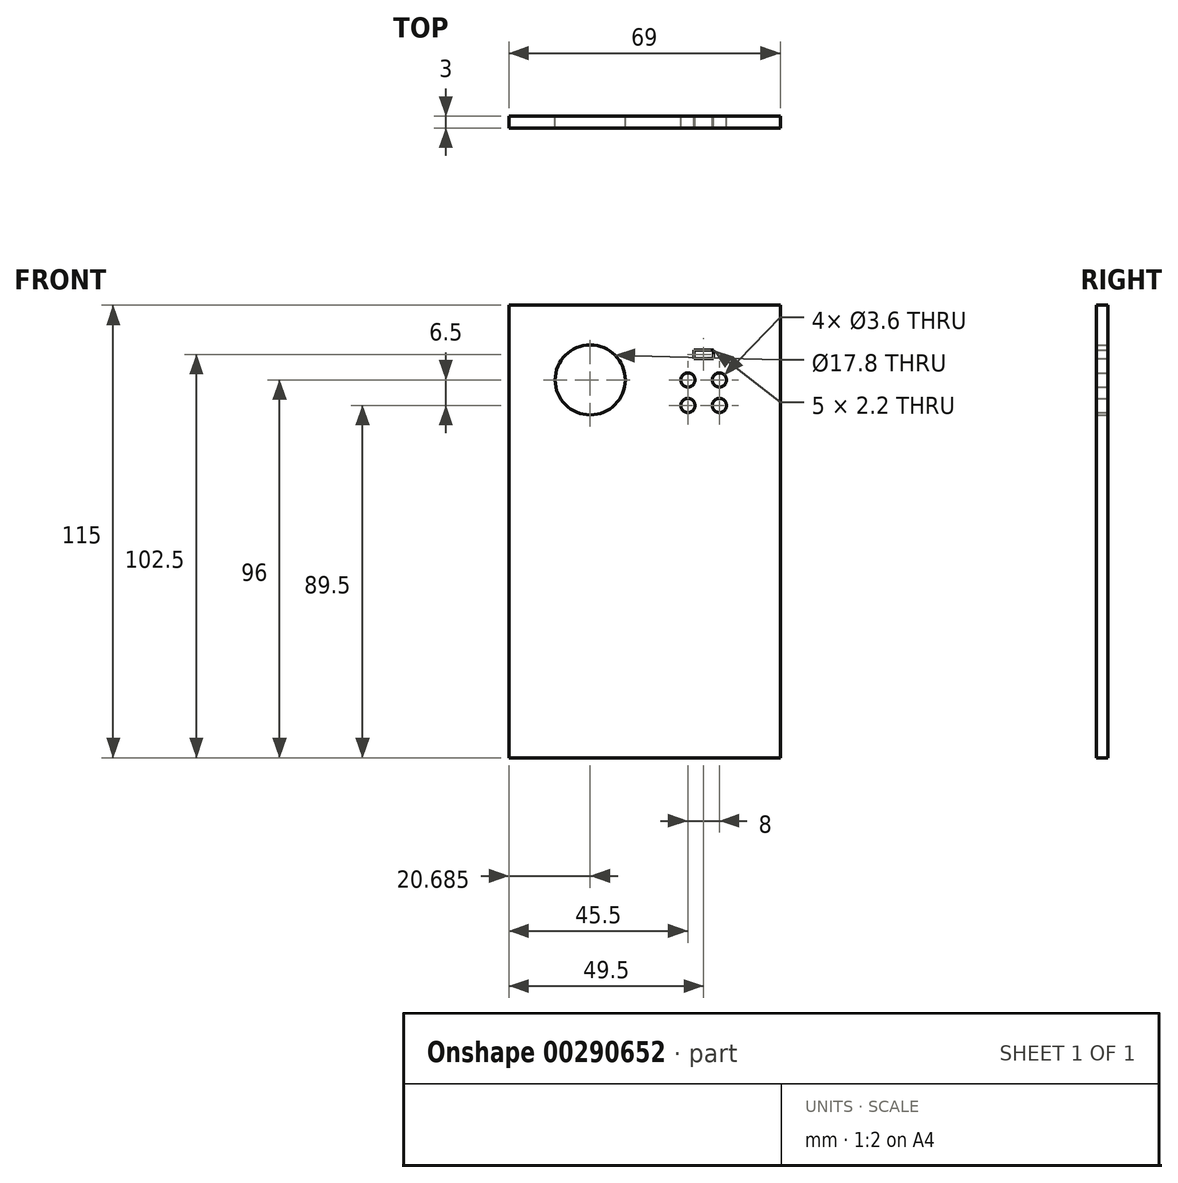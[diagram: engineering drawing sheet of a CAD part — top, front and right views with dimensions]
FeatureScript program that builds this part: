
annotation { "Feature Type Name" : "Feature", "Feature Type Description" : "" }
export const myFeature = defineFeature(function(context is Context, id is Id, definition is map)
    precondition{}
    {
        {
            var Q0;
            Q0=qCreatedBy(makeId("Front.planeOp"),FACE);
            var sketch = newSketch(context, id + "F0", { "sketchPlane" : qUnion([Q0])});
            skLineSegment(sketch, "E0", {"start": v(0, 0) * mm, "end": v(69, 0) * mm});
            skLineSegment(sketch, "E1", {"start": v(69, 0) * mm, "end": v(69, 115) * mm});
            skLineSegment(sketch, "E2", {"start": v(69, 115) * mm, "end": v(0, 115) * mm});
            skLineSegment(sketch, "E3", {"start": v(0, 115) * mm, "end": v(0, 0) * mm});
            skLineSegment(sketch, "E4.0", {"start": v(20.68, 108.31) * mm, "end": v(20.69, 84.1) * mm, "construction": true});
            skLineSegment(sketch, "E5.0", {"start": v(62.22, 96) * mm, "end": v(7.46, 96) * mm, "construction": true});
            skCircle(sketch, "E6", {"center": v(20.69, 96) * mm, "radius": 8.9 * mm});
            skLineSegment(sketch, "E7.0", {"start": v(62, 89.5) * mm, "end": v(41.78, 89.5) * mm, "construction": true});
            skLineSegment(sketch, "E8.0", {"start": v(53.5, 86.24) * mm, "end": v(53.5, 99.7) * mm, "construction": true});
            skPoint(sketch, "E9", {"position": v(53.5, 103.6) * mm});
            skLineSegment(sketch, "E10.0", {"start": v(53, 86.24) * mm, "end": v(53, 99.7) * mm, "construction": true});
            skLineSegment(sketch, "E11", {"start": v(45.5, 96) * mm, "end": v(45.5, 89.5) * mm, "construction": true});
            skLineSegment(sketch, "E12.0", {"start": v(45, 96) * mm, "end": v(45, 89.5) * mm, "construction": true});
            skCircle(sketch, "E13", {"center": v(45.5, 96) * mm, "radius": 1.8 * mm});
            skCircle(sketch, "E14", {"center": v(45.5, 89.5) * mm, "radius": 1.8 * mm});
            skCircle(sketch, "E15", {"center": v(53.5, 96) * mm, "radius": 1.8 * mm});
            skCircle(sketch, "E16", {"center": v(53.5, 89.5) * mm, "radius": 1.8 * mm});
            skLineSegment(sketch, "E17", {"start": v(52, 103.6) * mm, "end": v(52, 101.4) * mm});
            skLineSegment(sketch, "E18", {"start": v(52, 101.4) * mm, "end": v(47, 101.4) * mm});
            skLineSegment(sketch, "E19", {"start": v(47, 101.4) * mm, "end": v(47, 103.6) * mm});
            skLineSegment(sketch, "E20", {"start": v(47, 103.6) * mm, "end": v(52, 103.6) * mm});
            skLineSegment(sketch, "E21.0", {"start": v(49.5, 101.4) * mm, "end": v(49.5, 103.6) * mm, "construction": true});
            skSolve(sketch);
        }
        {
            var Q0;
            Q0=makeQuery(id+"F0.imprint","IMPRINT",FACE,{"disambiguationData":[TD([[makeQuery(id+"F0.imprint","IMPRINT",EDGE,{"derivedFrom":sQuery(id+"F0.wireOp",EDGE,"E0")}),1.0]])]});
            extrude(context, id + "F1", {"entities" : qUnion([Q0]), "depth" : 3 * mm});
        }
    });
